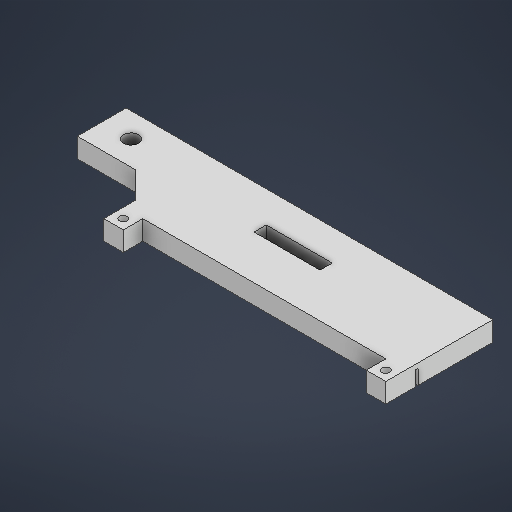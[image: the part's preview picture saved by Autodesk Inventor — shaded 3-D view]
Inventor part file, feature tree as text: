
AUTODESK INVENTOR PART (.ipt)
format: ipt  version: 2025 (Build 290162000, 162)  size: 292,352 bytes
history: native  units: mm
features: extrude x6, sketch x6, chamfer x2, projected_geometry x1
ambient origin geometry x8: Origin, YZ Plane, XZ Plane, XY Plane, X Axis, Y Axis, Z Axis, Center Point
bodies: Solid1 (feature_tree)
feature tree (15):
  extrude  "Extrusion1"  Depth=150.0mm
  extrude  "Extrusion2"  Depth=10.0mm
  extrude  "Extrusion3"  Depth=1.2mm
  extrude  "Extrusion4"  Depth=4.0mm
  extrude  "Extrusion5"  TaperAngle=45.0deg  [1 undecoded]
  extrude  "Extrusion6"  Depth=8.0mm
  chamfer  "Chamfer1"  Distance=8.0mm
  chamfer  "Chamfer2"  Distance=8.0mm
  sketch  "Sketch1"  dims[d3=20.0mm d4=150.0mm]
  sketch  "Sketch2"  dims[d7=10.0mm d8=6.2mm]
  projected_geometry  "Projected Loop1"
  sketch  "Sketch3"  dims[d9=6.0mm d10=0.0mm d11=1.2mm]
  sketch  "Sketch4"  dims[d12=2.0mm d13=0.0mm d14=4.0mm]
  sketch  "Sketch5"  dims[d15=2.0mm d16=0.0mm d18=45.0deg]
  sketch  "Sketch6"  dims[d19=8.0mm d20=8.0mm d21=8.0mm d22=8.0mm d23=3.2mm d24=3.2mm d25=10.0mm d26=0.0mm d27=11.5mm d28=7.0mm d29=23.0mm d30=29.5mm d31=6.0mm d32=6.0mm d33=3.2mm d34=3.2mm d35=6.0mm d36=0.0mm d37=6.0mm d38=2.5mm d39=20.0mm d40=5.0mm d41=18.75mm d42=0.0mm d43=7.0mm d44=2.0mm d45=45.0deg d46=1.0mm d47=2.0mm d48=45.0deg]
note: 1 required parameter value undecoded (feature->parameter linkage not recoverable at this tier; creation-order binding heuristic only, values carry confidence <= 0.55)
